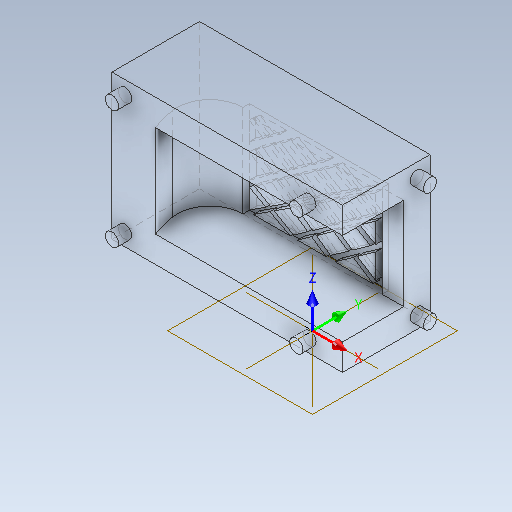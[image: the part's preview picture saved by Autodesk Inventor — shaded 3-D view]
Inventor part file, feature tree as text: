
AUTODESK INVENTOR PART (.ipt)
format: ipt  version: 2025.2 (Build 292293000, 293)  size: 696,320 bytes
history: native  units: mm
features: sketch x13, extrude x12, other x9, fillet x2, plane x1
ambient origin geometry x8: Origin, YZ Plane, XZ Plane, XY Plane, X Axis, Y Axis, Z Axis, Center Point
bodies: Volumenkörper2 (feature_tree), Volumenkörper3 (feature_tree)
feature tree (37):
  sketch  "Skizze1"  dims[d0=0.0mm d1=0.0mm d2=0.0mm d3=0.0mm d4=0.0mm d5=0.0mm d13=29.5mm d14=18.6mm d16=0.0mm d17=14.0mm]
  other  "BKS1"
  plane  "Arbeitsebene1"
  extrude  "Extrusion3"  Depth=14.0mm TaperAngle=0.0deg
  other  "Kombinieren1"
  extrude  "Extrusion9"  Depth=5.0mm
  extrude  "Extrusion10"  Depth=4.0mm
  extrude  "Extrusion11"  Depth=4.0mm
  extrude  "Extrusion12"  Depth=2.0mm TaperAngle=0.0deg
  extrude  "Extrusion13"  Depth=2.0mm TaperAngle=0.0deg
  extrude  "Extrusion14"  Depth=2.0mm
  extrude  "Extrusion15"  Depth=2.0mm
  extrude  "Extrusion16"  Depth=2.0mm
  extrude  "Extrusion17"  Depth=2.0mm
  extrude  "Extrusion19"  Depth=2.0mm
  sketch  "Skizze22"  dims[d42=35.0mm d43=0.0mm d52=4.0mm]
  sketch  "Skizze29"  dims[d53=4.0mm d54=4.0mm]
  sketch  "Skizze30"  dims[d55=4.0mm d62=2.0mm d63=0.0mm]
  sketch  "Skizze31"  dims[d64=2.0mm d65=0.0mm d66=2.0mm d67=0.0mm]
  sketch  "Skizze32"  dims[d68=2.0mm d69=0.0mm d70=2.0mm]
  sketch  "Skizze33"  dims[d71=2.0mm d73=2.0mm]
  sketch  "Skizze34"  dims[d74=2.0mm d76=2.0mm]
  sketch  "Skizze35"  dims[d77=2.0mm d80=2.0mm]
  sketch  "Skizze36"  dims[d82=2.0mm d83=2.0mm]
  sketch  "Skizze37"  dims[d84=2.0mm d85=2.0mm d86=2.0mm d87=40.0mm d88=0.0mm]
  sketch  "Skizze43"  dims[d90=2.0mm d91=0.0mm d92=2.0mm d93=0.0mm d94=2.0mm d95=0.0mm d96=2.0mm d97=0.0mm d98=2.0mm d99=2.0mm d100=2.0mm d101=2.0mm d102=2.0mm d103=2.0mm d104=2.0mm d105=2.0mm d106=5.0mm d107=2.0mm d108=2.0mm d109=5.0mm d111=14.0mm d114=9.3mm d115=9.3mm d150=0.8mm d153=0.8mm d154=0.996326mm d162=2.5mm d164=1.0mm d165=0.0mm d110=0.5mm d112=0.5mm d113=0.872665mm]
  other  "BKS1: YZ-Ebene"
  other  "BKS1: XZ-Ebene"
  other  "BKS1: XY-Ebene"
  other  "BKS1: X-Achse"
  other  "BKS1: Y-Achse"
  other  "BKS1: Z-Achse"
  other  "BKS1: Mittelpunkt"
  sketch  "Skizze3"  dims[d18=15.0mm d19=5.0mm]
  extrude  "Extrusion2"  Depth=2.0mm
  fillet  "Rundung4"  Radius=2.0mm
  fillet  "Rundung3"  Radius=40.0mm
